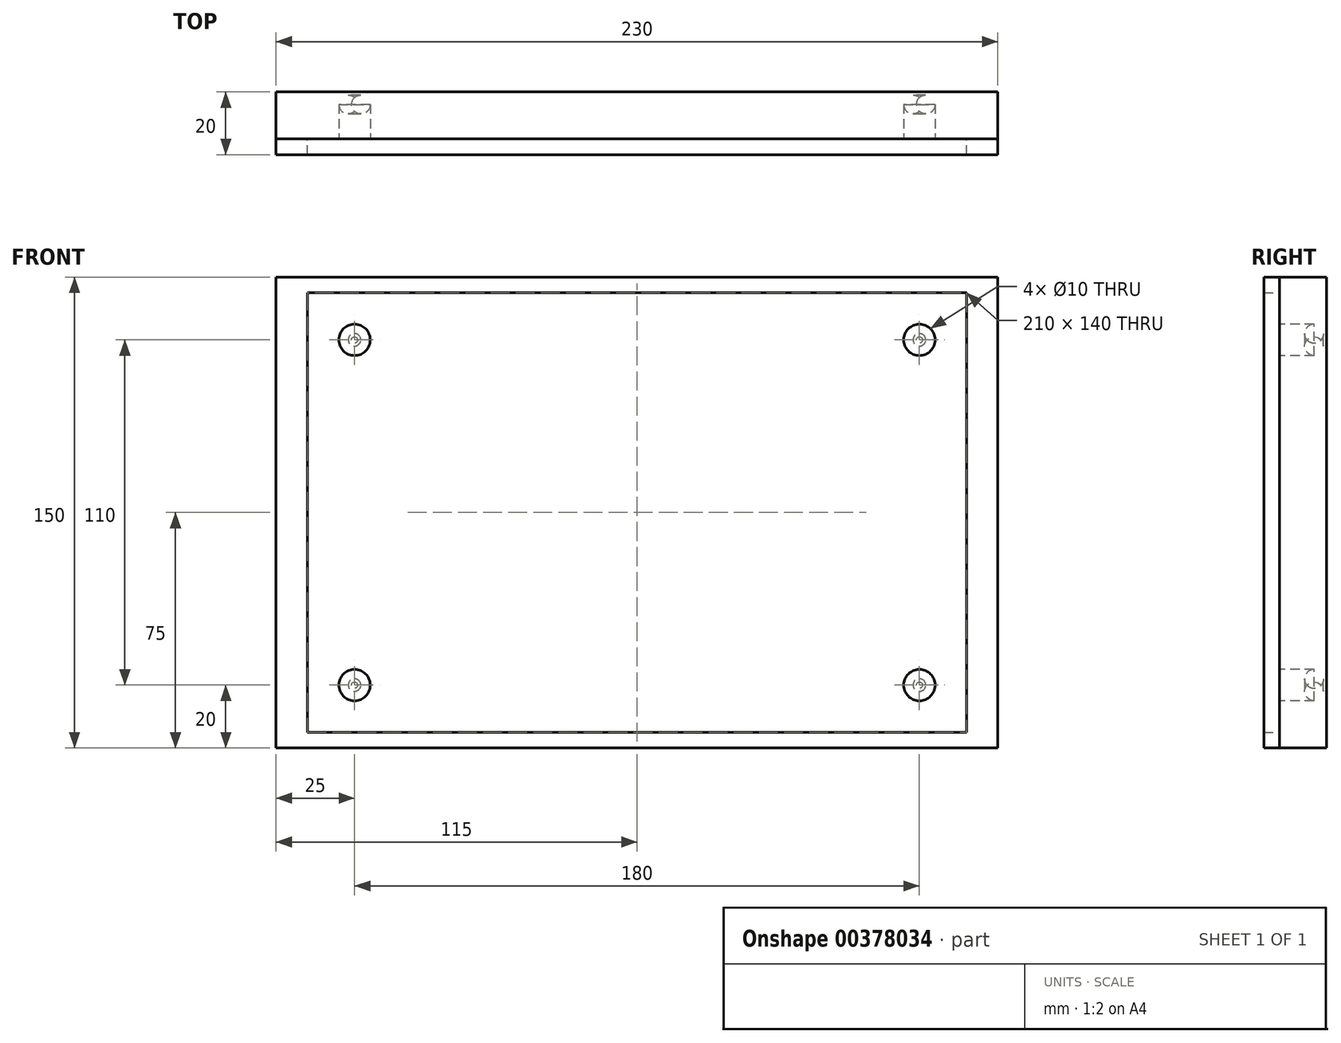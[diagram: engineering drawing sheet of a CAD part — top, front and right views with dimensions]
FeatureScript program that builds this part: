
annotation { "Feature Type Name" : "Feature", "Feature Type Description" : "" }
export const myFeature = defineFeature(function(context is Context, id is Id, definition is map)
    precondition{}
    {
        {
            var Q0;
            Q0=qCreatedBy(makeId("Front.planeOp"),FACE);
            var sketch = newSketch(context, id + "F0", { "sketchPlane" : qUnion([Q0])});
            skLineSegment(sketch, "E0.bottom", {"start": v(115, 75) * mm, "end": v(-115, 75) * mm});
            skLineSegment(sketch, "E0.top", {"start": v(115, -75) * mm, "end": v(-115, -75) * mm});
            skLineSegment(sketch, "E0.left", {"start": v(115, 75) * mm, "end": v(115, -75) * mm});
            skLineSegment(sketch, "E0.right", {"start": v(-115, 75) * mm, "end": v(-115, -75) * mm});
            skPoint(sketch, "E0.middle", {"position": v(0, 0) * mm});
            skLineSegment(sketch, "E1.bottom", {"start": v(105, 70) * mm, "end": v(-105, 70) * mm});
            skLineSegment(sketch, "E1.top", {"start": v(105, -70) * mm, "end": v(-105, -70) * mm});
            skLineSegment(sketch, "E1.left", {"start": v(105, 70) * mm, "end": v(105, -70) * mm});
            skLineSegment(sketch, "E1.right", {"start": v(-105, 70) * mm, "end": v(-105, -70) * mm});
            skCircle(sketch, "E2", {"center": v(-90, 55) * mm, "radius": 5 * mm});
            skCircle(sketch, "E3.0.1.0", {"center": v(-90, -55) * mm, "radius": 5 * mm});
            skCircle(sketch, "E3.1.0.0", {"center": v(90, 55) * mm, "radius": 5 * mm});
            skCircle(sketch, "E3.1.1.0", {"center": v(90, -55) * mm, "radius": 5 * mm});
            skLineSegment(sketch, "E3.direction1", {"start": v(-90, 55) * mm, "end": v(90, 55) * mm, "construction": true});
            skLineSegment(sketch, "E3.direction2", {"start": v(-90, 55) * mm, "end": v(-90, -55) * mm, "construction": true});
            skSolve(sketch);
        }
        {
            var Q0;
            Q0=makeQuery(id+"F0.imprint","IMPRINT",FACE,{"disambiguationData":[TD([[makeQuery(id+"F0.imprint","IMPRINT",EDGE,{"derivedFrom":sQuery(id+"F0.wireOp",EDGE,"E0.bottom")}),1.0]])]});
            extrude(context, id + "F1", {"entities" : qUnion([Q0]), "depth" : 5 * mm});
        }
        {
            var Q0;
            Q0=makeQuery(id+"F0.imprint","IMPRINT",FACE,{"disambiguationData":[TD([[makeQuery(id+"F0.imprint","IMPRINT",EDGE,{"derivedFrom":sQuery(id+"F0.wireOp",EDGE,"E1.bottom")}),1.0]])]});
            var Q1;
            Q1=makeQuery(id+"F0.imprint","IMPRINT",FACE,{"disambiguationData":[TD([[makeQuery(id+"F0.imprint","IMPRINT",EDGE,{"derivedFrom":sQuery(id+"F0.wireOp",EDGE,"E2")}),1.0]])]});
            var Q2;
            Q2=makeQuery(id+"F0.imprint","IMPRINT",FACE,{"disambiguationData":[TD([[makeQuery(id+"F0.imprint","IMPRINT",EDGE,{"derivedFrom":sQuery(id+"F0.wireOp",EDGE,"E3.0.1.0")}),1.0]])]});
            var Q3;
            Q3=makeQuery(id+"F0.imprint","IMPRINT",FACE,{"disambiguationData":[TD([[makeQuery(id+"F0.imprint","IMPRINT",EDGE,{"derivedFrom":sQuery(id+"F0.wireOp",EDGE,"E3.1.1.0")}),1.0]])]});
            var Q4;
            Q4=makeQuery(id+"F0.imprint","IMPRINT",FACE,{"disambiguationData":[TD([[makeQuery(id+"F0.imprint","IMPRINT",EDGE,{"derivedFrom":sQuery(id+"F0.wireOp",EDGE,"E3.1.0.0")}),1.0]])]});
            var Q5;
            Q5=makeQuery(id+"F0.imprint","IMPRINT",FACE,{"disambiguationData":[TD([[makeQuery(id+"F0.imprint","IMPRINT",EDGE,{"derivedFrom":sQuery(id+"F0.wireOp",EDGE,"E0.bottom")}),1.0]])]});
            extrude(context, id + "F2", {"entities" : qUnion([Q0, Q1, Q2, Q3, Q4, Q5]), "oppositeDirection" : true, "depth" : 15 * mm});
        }
        {
            var Q0;
            Q0=makeQuery(id+"F0.imprint","IMPRINT",FACE,{"disambiguationData":[TD([[makeQuery(id+"F0.imprint","IMPRINT",EDGE,{"derivedFrom":sQuery(id+"F0.wireOp",EDGE,"E2")}),1.0]])]});
            var Q1;
            Q1=makeQuery(id+"F0.imprint","IMPRINT",FACE,{"disambiguationData":[TD([[makeQuery(id+"F0.imprint","IMPRINT",EDGE,{"derivedFrom":sQuery(id+"F0.wireOp",EDGE,"E3.0.1.0")}),1.0]])]});
            var Q2;
            Q2=makeQuery(id+"F0.imprint","IMPRINT",FACE,{"disambiguationData":[TD([[makeQuery(id+"F0.imprint","IMPRINT",EDGE,{"derivedFrom":sQuery(id+"F0.wireOp",EDGE,"E3.1.1.0")}),1.0]])]});
            var Q3;
            Q3=makeQuery(id+"F0.imprint","IMPRINT",FACE,{"disambiguationData":[TD([[makeQuery(id+"F0.imprint","IMPRINT",EDGE,{"derivedFrom":sQuery(id+"F0.wireOp",EDGE,"E3.1.0.0")}),1.0]])]});
            extrude(context, id + "F3", {"entities" : qUnion([Q0, Q1, Q2, Q3]), "operationType" : NewBodyOperationType.REMOVE, "oppositeDirection" : true, "depth" : 14 * mm});
        }
        {
            var Q0;
            Q0=makeQuery(id+"F3.boolean.opBoolean","COPY",EDGE,{"derivedFrom":makeQuery(id+"F3.opExtrude","CAP_EDGE",EDGE,{"disambiguationData":[OSD([sQuery(id+"F0.wireOp",EDGE,"E2")])],"isStart":false})});
            var Q1;
            Q1=makeQuery(id+"F3.boolean.opBoolean","COPY",EDGE,{"derivedFrom":makeQuery(id+"F3.opExtrude","CAP_EDGE",EDGE,{"disambiguationData":[OSD([sQuery(id+"F0.wireOp",EDGE,"E3.0.1.0")])],"isStart":false})});
            var Q2;
            Q2=makeQuery(id+"F3.boolean.opBoolean","COPY",FACE,{"derivedFrom":makeQuery(id+"F3.opExtrude","CAP_FACE",FACE,{"disambiguationData":[OSD([sQuery(id+"F0.wireOp",EDGE,"E3.1.1.0")])],"isStart":false})});
            var Q3;
            Q3=makeQuery(id+"F3.boolean.opBoolean","COPY",FACE,{"derivedFrom":makeQuery(id+"F3.opExtrude","CAP_FACE",FACE,{"disambiguationData":[OSD([sQuery(id+"F0.wireOp",EDGE,"E3.1.0.0")])],"isStart":false})});
            fillet(context, id + "F4", {"entities" : qUnion([Q0, Q1, Q2, Q3]), "radius" : 3 * mm, "tangentPropagation" : true, "allowEdgeOverflow" : false});
        }
    });
